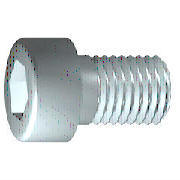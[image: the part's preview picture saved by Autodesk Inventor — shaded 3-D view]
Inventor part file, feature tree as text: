
AUTODESK INVENTOR PART (.ipt)
format: ipt  version: 2020 (Build 240168000, 168)  size: 196,608 bytes
history: native  units: mm (DEFAULTED — no unit token found)
features: sketch x2, extrude x1, plane x1, fillet x1
ambient origin geometry x7: Origin, YZ Plane, XY Plane, X Axis, Y Axis, Z Axis, Center Point
bodies: Solid1 (feature_tree)
feature tree (5):
  extrude  "슬롯"  Depth=10.0mm
  plane  "Work Plane1"
  fillet  "Fillet2"  Radius=0.49086mm
  sketch  "스케치1"
  sketch  "스케치2"
